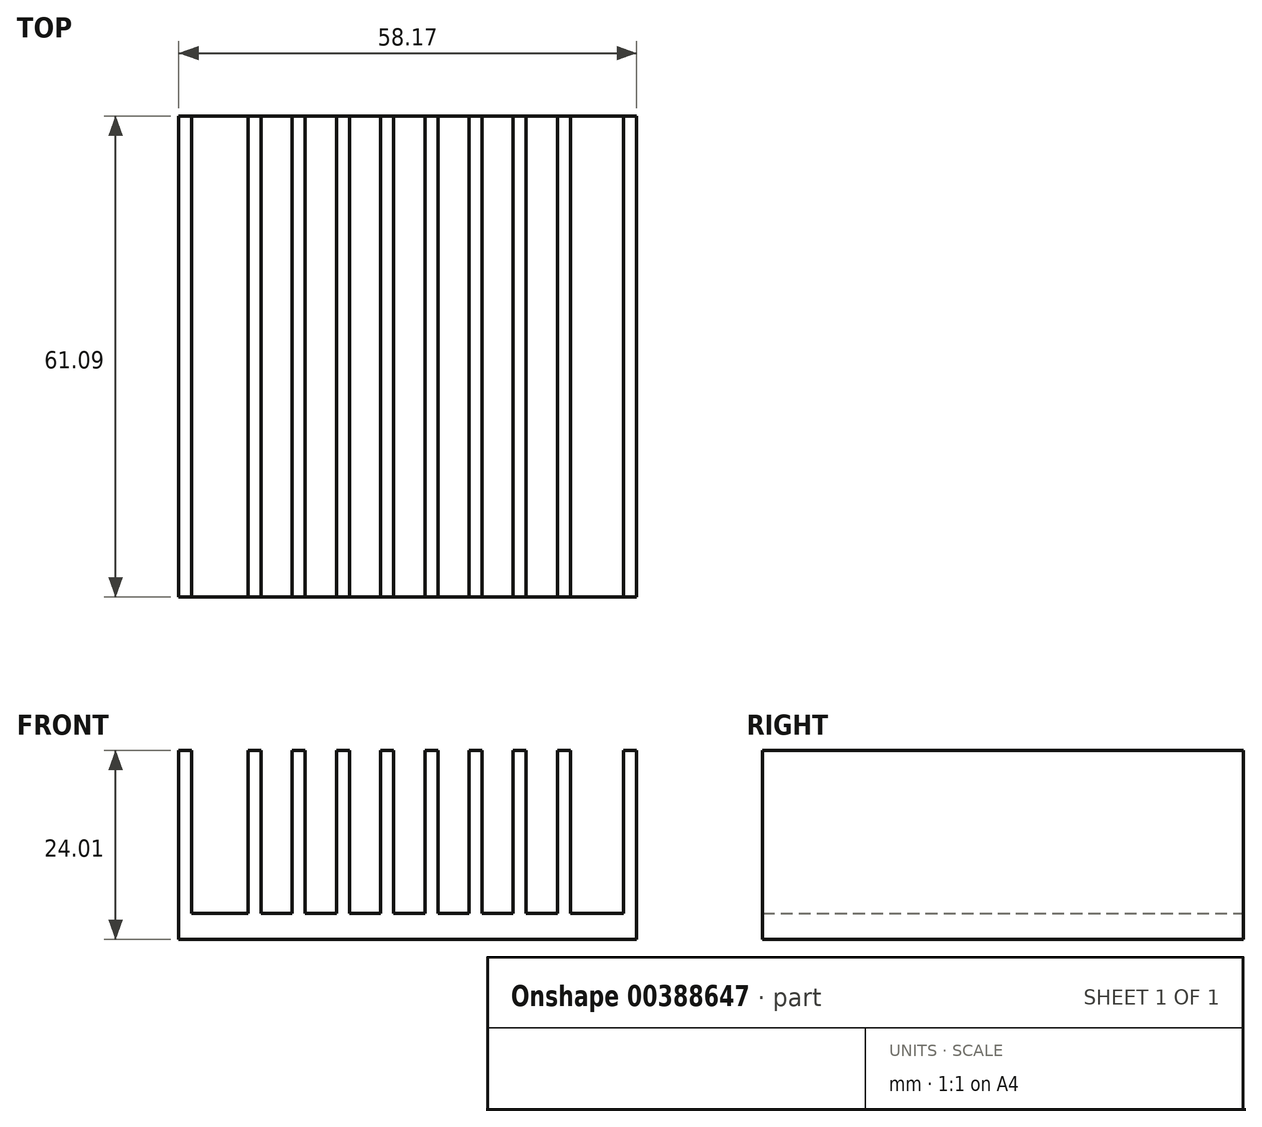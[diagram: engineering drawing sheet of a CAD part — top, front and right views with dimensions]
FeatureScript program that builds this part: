
annotation { "Feature Type Name" : "Feature", "Feature Type Description" : "" }
export const myFeature = defineFeature(function(context is Context, id is Id, definition is map)
    precondition{}
    {
        {
            var Q0;
            Q0=qCreatedBy(makeId("Front.planeOp"),FACE);
            var sketch = newSketch(context, id + "F0", { "sketchPlane" : qUnion([Q0])});
            skLineSegment(sketch, "E0.bottom", {"start": v(-16.08, 37.74) * mm, "end": v(42.09, 37.74) * mm});
            skLineSegment(sketch, "E0.top", {"start": v(-16.08, 13.73) * mm, "end": v(42.09, 13.73) * mm});
            skLineSegment(sketch, "E0.left", {"start": v(-16.08, 37.74) * mm, "end": v(-16.08, 13.73) * mm});
            skLineSegment(sketch, "E0.right", {"start": v(42.09, 37.74) * mm, "end": v(42.09, 13.73) * mm});
            skLineSegment(sketch, "E1.bottom", {"start": v(-14.43, 37.74) * mm, "end": v(-7.26, 37.74) * mm});
            skLineSegment(sketch, "E1.top", {"start": v(-14.43, 17.03) * mm, "end": v(-7.26, 17.03) * mm});
            skLineSegment(sketch, "E1.left", {"start": v(-14.43, 37.74) * mm, "end": v(-14.43, 17.03) * mm});
            skLineSegment(sketch, "E1.right", {"start": v(-7.26, 37.74) * mm, "end": v(-7.26, 17.03) * mm});
            skLineSegment(sketch, "E2.bottom", {"start": v(-5.61, 37.74) * mm, "end": v(-1.65, 37.74) * mm});
            skLineSegment(sketch, "E2.top", {"start": v(-5.61, 17.03) * mm, "end": v(-1.65, 17.03) * mm});
            skLineSegment(sketch, "E2.left", {"start": v(-5.61, 37.74) * mm, "end": v(-5.61, 17.03) * mm});
            skLineSegment(sketch, "E2.right", {"start": v(-1.65, 37.74) * mm, "end": v(-1.65, 17.03) * mm});
            skLineSegment(sketch, "E3.bottom", {"start": v(0, 37.74) * mm, "end": v(3.96, 37.74) * mm});
            skLineSegment(sketch, "E3.top", {"start": v(0, 17.03) * mm, "end": v(3.96, 17.03) * mm});
            skLineSegment(sketch, "E3.left", {"start": v(0, 37.74) * mm, "end": v(0, 17.03) * mm});
            skLineSegment(sketch, "E3.right", {"start": v(3.96, 37.74) * mm, "end": v(3.96, 17.03) * mm});
            skLineSegment(sketch, "E4.bottom", {"start": v(5.61, 37.74) * mm, "end": v(9.58, 37.74) * mm});
            skLineSegment(sketch, "E4.top", {"start": v(5.61, 17.03) * mm, "end": v(9.58, 17.03) * mm});
            skLineSegment(sketch, "E4.left", {"start": v(5.61, 37.74) * mm, "end": v(5.61, 17.03) * mm});
            skLineSegment(sketch, "E4.right", {"start": v(9.58, 37.74) * mm, "end": v(9.58, 17.03) * mm});
            skLineSegment(sketch, "E5.bottom", {"start": v(11.23, 37.74) * mm, "end": v(15.19, 37.74) * mm});
            skLineSegment(sketch, "E5.top", {"start": v(11.23, 17.03) * mm, "end": v(15.19, 17.03) * mm});
            skLineSegment(sketch, "E5.left", {"start": v(11.23, 37.74) * mm, "end": v(11.23, 17.03) * mm});
            skLineSegment(sketch, "E5.right", {"start": v(15.19, 37.74) * mm, "end": v(15.19, 17.03) * mm});
            skLineSegment(sketch, "E6.bottom", {"start": v(16.84, 37.74) * mm, "end": v(20.8, 37.74) * mm});
            skLineSegment(sketch, "E6.top", {"start": v(16.84, 17.03) * mm, "end": v(20.8, 17.03) * mm});
            skLineSegment(sketch, "E6.left", {"start": v(16.84, 37.74) * mm, "end": v(16.84, 17.03) * mm});
            skLineSegment(sketch, "E6.right", {"start": v(20.8, 37.74) * mm, "end": v(20.8, 17.03) * mm});
            skLineSegment(sketch, "E7.bottom", {"start": v(22.45, 37.74) * mm, "end": v(26.42, 37.74) * mm});
            skLineSegment(sketch, "E7.top", {"start": v(22.45, 17.03) * mm, "end": v(26.42, 17.03) * mm});
            skLineSegment(sketch, "E7.left", {"start": v(22.45, 37.74) * mm, "end": v(22.45, 17.03) * mm});
            skLineSegment(sketch, "E7.right", {"start": v(26.42, 37.74) * mm, "end": v(26.42, 17.03) * mm});
            skLineSegment(sketch, "E8.bottom", {"start": v(28.07, 37.74) * mm, "end": v(32.03, 37.74) * mm});
            skLineSegment(sketch, "E8.top", {"start": v(28.07, 17.03) * mm, "end": v(32.03, 17.03) * mm});
            skLineSegment(sketch, "E8.left", {"start": v(28.07, 37.74) * mm, "end": v(28.07, 17.03) * mm});
            skLineSegment(sketch, "E8.right", {"start": v(32.03, 37.74) * mm, "end": v(32.03, 17.03) * mm});
            skLineSegment(sketch, "E9.bottom", {"start": v(33.68, 37.74) * mm, "end": v(40.44, 37.74) * mm});
            skLineSegment(sketch, "E9.top", {"start": v(33.68, 17.03) * mm, "end": v(40.44, 17.03) * mm});
            skLineSegment(sketch, "E9.left", {"start": v(33.68, 37.74) * mm, "end": v(33.68, 17.03) * mm});
            skLineSegment(sketch, "E9.right", {"start": v(40.44, 37.74) * mm, "end": v(40.44, 17.03) * mm});
            skSolve(sketch);
        }
        {
            var Q0;
            Q0=makeQuery(id+"F0.imprint","IMPRINT",FACE,{"disambiguationData":[TD([[makeQuery(id+"F0.imprint","IMPRINT",EDGE,{"derivedFrom":sQuery(id+"F0.wireOp",EDGE,"E0.top")}),1.0]])]});
            extrude(context, id + "F1", {"entities" : qUnion([Q0]), "depth" : 61.1 * mm});
        }
    });
